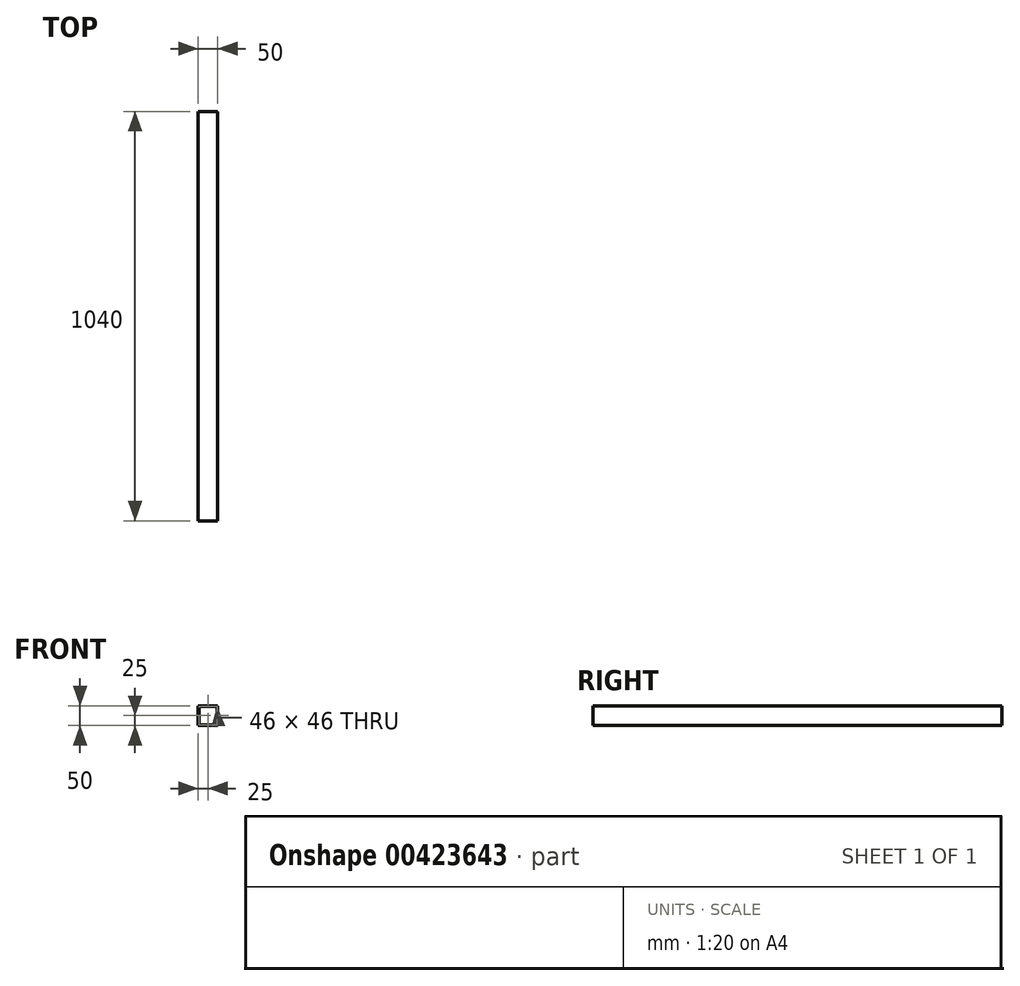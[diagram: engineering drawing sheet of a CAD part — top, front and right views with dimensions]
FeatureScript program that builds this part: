
annotation { "Feature Type Name" : "Feature", "Feature Type Description" : "" }
export const myFeature = defineFeature(function(context is Context, id is Id, definition is map)
    precondition{}
    {
        {
            var Q0;
            Q0=qCreatedBy(makeId("Front.planeOp"),FACE);
            var sketch = newSketch(context, id + "F0", { "sketchPlane" : qUnion([Q0])});
            skLineSegment(sketch, "E0.bottom", {"start": v(0, 0) * mm, "end": v(-50, 0) * mm});
            skLineSegment(sketch, "E0.top", {"start": v(0, 50) * mm, "end": v(-50, 50) * mm});
            skLineSegment(sketch, "E0.left", {"start": v(0, 0) * mm, "end": v(0, 50) * mm});
            skLineSegment(sketch, "E0.right", {"start": v(-50, 0) * mm, "end": v(-50, 50) * mm});
            skLineSegment(sketch, "E1.0", {"start": v(-2, 48) * mm, "end": v(-48, 48) * mm});
            skLineSegment(sketch, "E1.1", {"start": v(-2, 2) * mm, "end": v(-2, 48) * mm});
            skLineSegment(sketch, "E1.2", {"start": v(-2, 2) * mm, "end": v(-48, 2) * mm});
            skLineSegment(sketch, "E1.3", {"start": v(-48, 2) * mm, "end": v(-48, 48) * mm});
            skSolve(sketch);
        }
        {
            var Q0;
            Q0=makeQuery(id+"F0.imprint","IMPRINT",FACE,{"disambiguationData":[TD([[makeQuery(id+"F0.imprint","IMPRINT",EDGE,{"derivedFrom":sQuery(id+"F0.wireOp",EDGE,"E0.bottom")}),-1.0]])]});
            extrude(context, id + "F1", {"entities" : qUnion([Q0]), "depth" : (1010 + (65 * 2) - 100) * mm});
        }
    });
